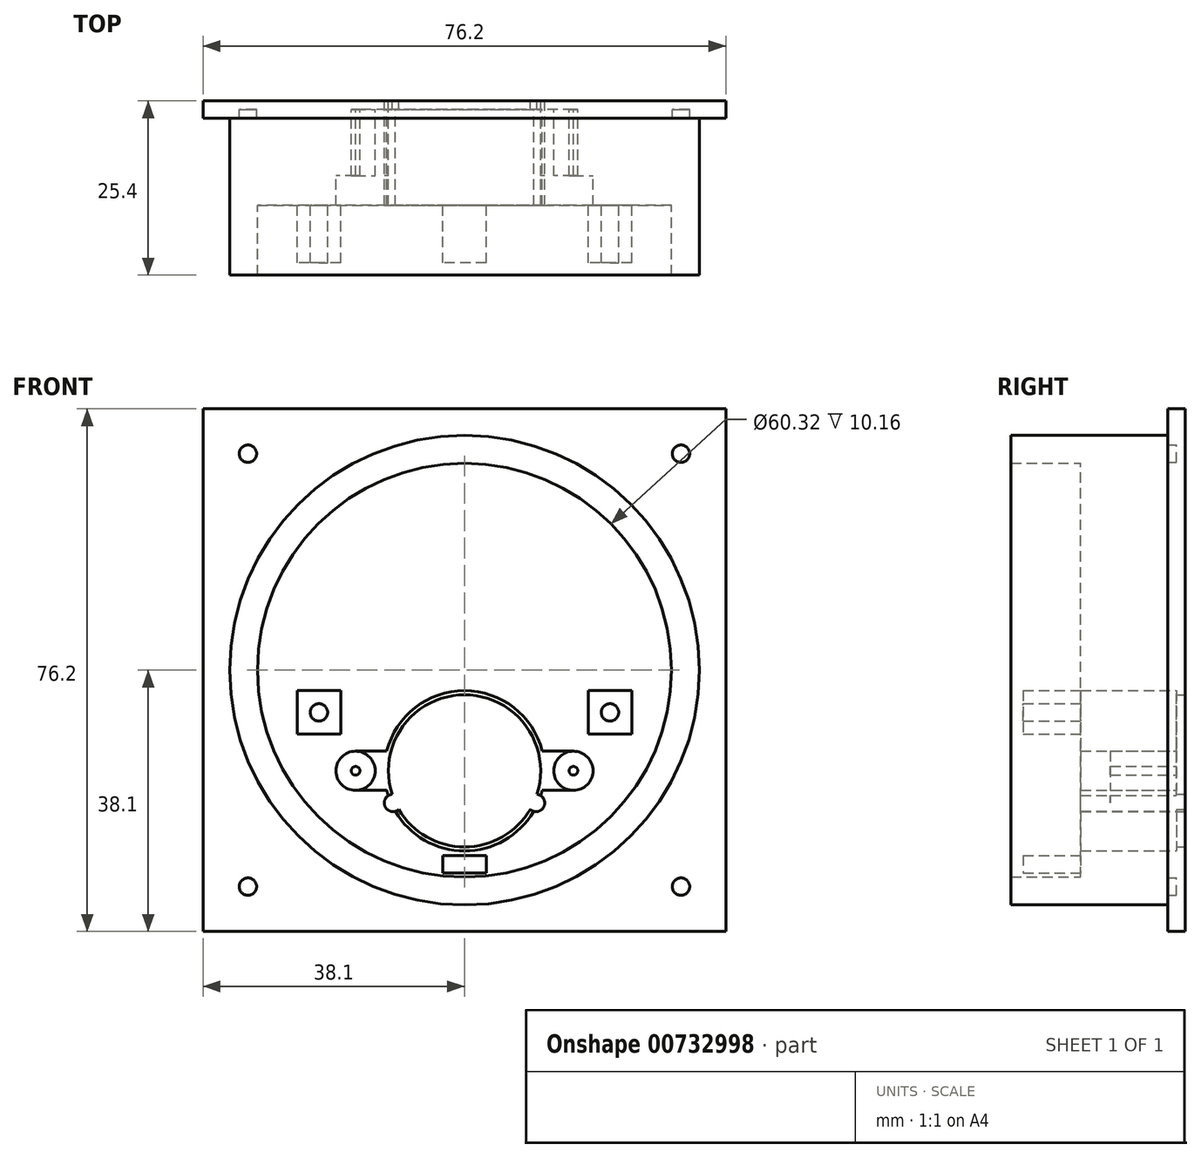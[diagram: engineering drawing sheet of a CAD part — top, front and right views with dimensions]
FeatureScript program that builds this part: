
annotation { "Feature Type Name" : "Feature", "Feature Type Description" : "" }
export const myFeature = defineFeature(function(context is Context, id is Id, definition is map)
    precondition{}
    {
        {
            var Q0;
            Q0=qCreatedBy(makeId("Front.planeOp"),FACE);
            var sketch = newSketch(context, id + "F0", { "sketchPlane" : qUnion([Q0])});
            skCircle(sketch, "E0", {"center": v(0, 0) * mm, "radius": 30.16 * mm});
            skCircle(sketch, "E1", {"center": v(0, -14.67) * mm, "radius": 11.68 * mm});
            skCircle(sketch, "E2", {"center": v(-15.88, -14.67) * mm, "radius": 2.86 * mm});
            skCircle(sketch, "E3", {"center": v(15.88, -14.67) * mm, "radius": 2.86 * mm});
            skPoint(sketch, "E4", {"position": v(-10.41, -19.34) * mm});
            skPoint(sketch, "E5", {"position": v(10.41, -19.34) * mm});
            skLineSegment(sketch, "E6.bottom", {"start": v(15.88, -11.81) * mm, "end": v(-15.88, -11.81) * mm});
            skLineSegment(sketch, "E6.top", {"start": v(15.88, -17.53) * mm, "end": v(-15.88, -17.53) * mm});
            skLineSegment(sketch, "E6.left", {"start": v(15.88, -11.81) * mm, "end": v(15.88, -17.53) * mm});
            skLineSegment(sketch, "E6.right", {"start": v(-15.88, -11.81) * mm, "end": v(-15.88, -17.53) * mm});
            skLineSegment(sketch, "E7.bottom", {"start": v(38.1, 38.1) * mm, "end": v(-38.1, 38.1) * mm});
            skLineSegment(sketch, "E7.top", {"start": v(38.1, -38.1) * mm, "end": v(-38.1, -38.1) * mm});
            skLineSegment(sketch, "E7.left", {"start": v(38.1, 38.1) * mm, "end": v(38.1, -38.1) * mm});
            skLineSegment(sketch, "E7.right", {"start": v(-38.1, 38.1) * mm, "end": v(-38.1, -38.1) * mm});
            skPoint(sketch, "E8", {"position": v(-31.56, 31.56) * mm});
            skPoint(sketch, "E9", {"position": v(31.56, 31.56) * mm});
            skPoint(sketch, "E10", {"position": v(31.56, -31.56) * mm});
            skPoint(sketch, "E11", {"position": v(-31.56, -31.56) * mm});
            skSolve(sketch);
        }
        {
            var Q0;
            Q0=makeQuery(id+"F0.imprint","IMPRINT",FACE,{"disambiguationData":[TD([[makeQuery(id+"F0.imprint","IMPRINT",EDGE,{"derivedFrom":sQuery(id+"F0.wireOp",EDGE,"E0")}),1.0]])]});
            extrude(context, id + "F1", {"entities" : qUnion([Q0]), "depth" : 15.24 * mm, "offsetDistance" : 25.4 * mm});
        }
        {
            var Q0;
            Q0=sQuery(id+"F0.wireOp",VERTEX,"E4");
            var Q1;
            Q1=sQuery(id+"F0.wireOp",VERTEX,"E5");
            var Q2;
            Q2=makeQuery(id+"F1.opExtrude","SWEPT_BODY",BODY,{"disambiguationData":[OSD([sQuery(id+"F0.wireOp",EDGE,"E0"),sQuery(id+"F0.wireOp",EDGE,"E1"),sQuery(id+"F0.wireOp",EDGE,"E2"),sQuery(id+"F0.wireOp",EDGE,"E3"),sQuery(id+"F0.wireOp",EDGE,"AQVEhfqM-bFfV-HZmN-Bbqf-DNwuXJOXuMRX.top"),sQuery(id+"F0.wireOp",EDGE,"FJdyEDiO-yEiY-Ot4F-tMeN-V1f38BCFD4gc.top")])]});
            hole(context, id + "F2", {"style" : HoleStyle.SIMPLE, "endStyle" : HoleEndStyle.THROUGH, "oppositeDirection" : true, "holeDiameter" : 2.54 * mm, "majorDiameter" : 6.35 * mm, "isTappedThrough" : true, "tappedDepth" : 12.7 * mm, "tapClearance" : 3, "locations" : qUnion([Q0, Q1]), "scope" : qUnion([Q2])});
        }
        {
            var Q0;
            {var subQ4=sQuery(id+"F0.wireOp",EDGE,"E6.right");Q0=makeQuery(id+"F0.imprint","IMPRINT",FACE,{"disambiguationData":[TD([[makeQuery(id+"F0.imprint","IMPRINT",EDGE,{"derivedFrom":subQ4}),1.0]])]});}
            var Q1;
            {var subQ0=sQuery(id+"F0.wireOp",EDGE,"E6.right");Q1=makeQuery(id+"F0.imprint","IMPRINT",FACE,{"disambiguationData":[TD([[makeQuery(id+"F0.imprint","IMPRINT",EDGE,{"derivedFrom":subQ0}),-1.0]])]});}
            var Q2;
            {var subQ4=sQuery(id+"F0.wireOp",EDGE,"E6.left");Q2=makeQuery(id+"F0.imprint","IMPRINT",FACE,{"disambiguationData":[TD([[makeQuery(id+"F0.imprint","IMPRINT",EDGE,{"derivedFrom":subQ4}),-1.0]])]});}
            var Q3;
            {var subQ0=sQuery(id+"F0.wireOp",EDGE,"E6.left");Q3=makeQuery(id+"F0.imprint","IMPRINT",FACE,{"disambiguationData":[TD([[makeQuery(id+"F0.imprint","IMPRINT",EDGE,{"derivedFrom":subQ0}),1.0]])]});}
            var Q4;
            {var subQ0=sQuery(id+"F0.wireOp",EDGE,"E6.bottom");var subQ1=sQuery(id+"F0.wireOp",EDGE,"E1");var subQ2=makeQuery(id+"F0.imprint","INTERSECT",VERTEX,{"disambiguationData":[OD(0.0)],"derivedFrom":[subQ1,subQ0]});Q4=makeQuery(id+"F0.imprint","IMPRINT",FACE,{"disambiguationData":[TD([[makeQuery(id+"F0.imprint","IMPRINT",EDGE,{"disambiguationData":[TD([[subQ2,-1.0]])],"derivedFrom":subQ1}),-1.0]])]});}
            var Q5;
            {var subQ0=sQuery(id+"F0.wireOp",EDGE,"E6.bottom");var subQ1=sQuery(id+"F0.wireOp",EDGE,"E1");var subQ2=makeQuery(id+"F0.imprint","INTERSECT",VERTEX,{"disambiguationData":[OD(1.0)],"derivedFrom":[subQ1,subQ0]});Q5=makeQuery(id+"F0.imprint","IMPRINT",FACE,{"disambiguationData":[TD([[makeQuery(id+"F0.imprint","IMPRINT",EDGE,{"disambiguationData":[TD([[subQ2,1.0]])],"derivedFrom":subQ1}),-1.0]])]});}
            extrude(context, id + "F3", {"entities" : qUnion([Q0, Q1, Q2, Q3, Q4, Q5]), "operationType" : NewBodyOperationType.ADD, "depth" : 10.92 * mm, "offsetDistance" : 25.4 * mm});
        }
        {
            var Q0;
            Q0=sQuery(id+"F0.wireOp",VERTEX,"E2.center");
            var Q1;
            Q1=sQuery(id+"F0.wireOp",VERTEX,"E3.center");
            var Q2;
            Q2=makeQuery(id+"F1.opExtrude","SWEPT_BODY",BODY,{"disambiguationData":[OSD([sQuery(id+"F0.wireOp",EDGE,"E0"),sQuery(id+"F0.wireOp",EDGE,"E1"),sQuery(id+"F0.wireOp",EDGE,"E2"),sQuery(id+"F0.wireOp",EDGE,"E3"),sQuery(id+"F0.wireOp",EDGE,"E6.bottom"),sQuery(id+"F0.wireOp",EDGE,"E6.top")])]});
            hole(context, id + "F4", {"style" : HoleStyle.SIMPLE, "endStyle" : HoleEndStyle.THROUGH, "oppositeDirection" : true, "holeDiameter" : 1.27 * mm, "majorDiameter" : 6.35 * mm, "isTappedThrough" : true, "tappedDepth" : 12.7 * mm, "tapClearance" : 3, "locations" : qUnion([Q0, Q1]), "scope" : qUnion([Q2])});
        }
        {
            var Q0;
            Q0=qCreatedBy(makeId("Front.planeOp"),FACE);
            var sketch = newSketch(context, id + "F5", { "sketchPlane" : qUnion([Q0])});
            skCircle(sketch, "E12", {"center": v(0, 0) * mm, "radius": 30.16 * mm});
            skCircle(sketch, "E13", {"center": v(0, 0) * mm, "radius": 34.23 * mm});
            skSolve(sketch);
        }
        {
            var Q0;
            Q0 = qSketchRegion(id + "F5", true);
            extrude(context, id + "F6", {"entities" : qUnion([Q0]), "operationType" : NewBodyOperationType.ADD, "depth" : 25.4 * mm, "offsetDistance" : 25.4 * mm});
        }
        {
            var Q0;
            Q0=qCreatedBy(makeId("Front.planeOp"),FACE);
            cPlane(context, id + "F7", {"entities" : qUnion([Q0]), "cplaneType" : CPlaneType.OFFSET, "offset" : 15.24 * mm, "width" : 152.4 * mm, "height" : 152.4 * mm});
        }
        {
            var Q0;
            Q0=qCreatedBy(id+"F7.planeOp",FACE);
            var sketch = newSketch(context, id + "F8", { "sketchPlane" : qUnion([Q0])});
            skLineSegment(sketch, "E14.bottom", {"start": v(3.18, -27.01) * mm, "end": v(-3.18, -27.01) * mm});
            skLineSegment(sketch, "E14.top", {"start": v(3.18, -29.55) * mm, "end": v(-3.18, -29.55) * mm});
            skLineSegment(sketch, "E14.left", {"start": v(3.18, -27.01) * mm, "end": v(3.18, -29.55) * mm});
            skLineSegment(sketch, "E14.right", {"start": v(-3.18, -27.01) * mm, "end": v(-3.18, -29.55) * mm});
            skPoint(sketch, "E14.middle", {"position": v(0, -28.28) * mm});
            skLineSegment(sketch, "E15.bottom", {"start": v(-18.03, -2.98) * mm, "end": v(-24.38, -2.98) * mm});
            skLineSegment(sketch, "E15.top", {"start": v(-18.03, -9.33) * mm, "end": v(-24.38, -9.33) * mm});
            skLineSegment(sketch, "E15.left", {"start": v(-18.03, -2.98) * mm, "end": v(-18.03, -9.33) * mm});
            skLineSegment(sketch, "E15.right", {"start": v(-24.38, -2.98) * mm, "end": v(-24.38, -9.33) * mm});
            skPoint(sketch, "E15.middle", {"position": v(-21.2, -6.16) * mm});
            skLineSegment(sketch, "E16.bottom", {"start": v(24.38, -9.33) * mm, "end": v(18.03, -9.33) * mm});
            skLineSegment(sketch, "E16.top", {"start": v(24.38, -2.98) * mm, "end": v(18.03, -2.98) * mm});
            skLineSegment(sketch, "E16.left", {"start": v(24.38, -9.33) * mm, "end": v(24.38, -2.98) * mm});
            skLineSegment(sketch, "E16.right", {"start": v(18.03, -9.33) * mm, "end": v(18.03, -2.98) * mm});
            skPoint(sketch, "E16.middle", {"position": v(21.2, -6.16) * mm});
            skSolve(sketch);
        }
        {
            var Q0;
            Q0 = qSketchRegion(id + "F8", true);
            extrude(context, id + "F9", {"entities" : qUnion([Q0]), "operationType" : NewBodyOperationType.ADD, "depth" : 8.38 * mm, "offsetDistance" : 25.4 * mm});
        }
        {
            var Q0;
            Q0=sQuery(id+"F8.wireOp",VERTEX,"E15.middle");
            var Q1;
            Q1=sQuery(id+"F8.wireOp",VERTEX,"E16.middle");
            var Q2;
            Q2=makeQuery(id+"F1.opExtrude","SWEPT_BODY",BODY,{"disambiguationData":[OSD([sQuery(id+"F0.wireOp",EDGE,"E0"),sQuery(id+"F0.wireOp",EDGE,"E1"),sQuery(id+"F0.wireOp",EDGE,"E2"),sQuery(id+"F0.wireOp",EDGE,"E3"),sQuery(id+"F0.wireOp",EDGE,"E6.bottom"),sQuery(id+"F0.wireOp",EDGE,"E6.top")])]});
            hole(context, id + "F10", {"style" : HoleStyle.SIMPLE, "endStyle" : HoleEndStyle.THROUGH, "oppositeDirection" : true, "holeDiameter" : 2.54 * mm, "majorDiameter" : 6.35 * mm, "isTappedThrough" : true, "tappedDepth" : 12.7 * mm, "tapClearance" : 3, "locations" : qUnion([Q0, Q1]), "scope" : qUnion([Q2])});
        }
        {
            var Q0;
            Q0=makeQuery(id+"F0.imprint","IMPRINT",FACE,{"disambiguationData":[TD([[makeQuery(id+"F0.imprint","IMPRINT",EDGE,{"derivedFrom":sQuery(id+"F0.wireOp",EDGE,"E0")}),-1.0]])]});
            extrude(context, id + "F11", {"entities" : qUnion([Q0]), "operationType" : NewBodyOperationType.ADD, "depth" : 2.54 * mm, "offsetDistance" : 25.4 * mm});
        }
        {
            var Q0;
            Q0=sQuery(id+"F0.wireOp",VERTEX,"E10");
            var Q1;
            Q1=sQuery(id+"F0.wireOp",VERTEX,"E11");
            var Q2;
            Q2=sQuery(id+"F0.wireOp",VERTEX,"E8");
            var Q3;
            Q3=sQuery(id+"F0.wireOp",VERTEX,"E9");
            var Q4;
            Q4=makeQuery(id+"F1.opExtrude","SWEPT_BODY",BODY,{"disambiguationData":[OSD([sQuery(id+"F0.wireOp",EDGE,"E0"),sQuery(id+"F0.wireOp",EDGE,"E1"),sQuery(id+"F0.wireOp",EDGE,"E2"),sQuery(id+"F0.wireOp",EDGE,"E3"),sQuery(id+"F0.wireOp",EDGE,"E6.bottom"),sQuery(id+"F0.wireOp",EDGE,"E6.top")])]});
            hole(context, id + "F12", {"style" : HoleStyle.SIMPLE, "endStyle" : HoleEndStyle.THROUGH, "oppositeDirection" : true, "holeDiameter" : 2.54 * mm, "majorDiameter" : 6.35 * mm, "isTappedThrough" : true, "tappedDepth" : 12.7 * mm, "tapClearance" : 3, "locations" : qUnion([Q0, Q1, Q2, Q3]), "scope" : qUnion([Q4])});
        }
        {
            var Q0;
            Q0=qCreatedBy(makeId("Front.planeOp"),FACE);
            var sketch = newSketch(context, id + "F13", { "sketchPlane" : qUnion([Q0])});
            skLineSegment(sketch, "E17.bottom", {"start": v(38.1, 38.1) * mm, "end": v(-38.1, 38.1) * mm});
            skLineSegment(sketch, "E17.top", {"start": v(38.1, -38.1) * mm, "end": v(-38.1, -38.1) * mm});
            skLineSegment(sketch, "E17.left", {"start": v(38.1, 38.1) * mm, "end": v(38.1, -38.1) * mm});
            skLineSegment(sketch, "E17.right", {"start": v(-38.1, 38.1) * mm, "end": v(-38.1, -38.1) * mm});
            skCircle(sketch, "E18", {"center": v(0, -14.68) * mm, "radius": 11.1 * mm});
            skPoint(sketch, "E19", {"position": v(10.41, -19.35) * mm});
            skPoint(sketch, "E20", {"position": v(-10.41, -19.35) * mm});
            skSolve(sketch);
        }
        {
            var Q0;
            Q0 = qSketchRegion(id + "F13", true);
            extrude(context, id + "F14", {"entities" : qUnion([Q0]), "operationType" : NewBodyOperationType.ADD, "depth" : 1.27 * mm, "offsetDistance" : 25.4 * mm});
        }
        {
            var Q0;
            Q0=sQuery(id+"F13.wireOp",VERTEX,"E19");
            var Q1;
            Q1=sQuery(id+"F13.wireOp",VERTEX,"E20");
            var Q2;
            Q2=makeQuery(id+"F1.opExtrude","SWEPT_BODY",BODY,{"disambiguationData":[OSD([sQuery(id+"F0.wireOp",EDGE,"E0"),sQuery(id+"F0.wireOp",EDGE,"E1"),sQuery(id+"F0.wireOp",EDGE,"E2"),sQuery(id+"F0.wireOp",EDGE,"E3"),sQuery(id+"F0.wireOp",EDGE,"E6.bottom"),sQuery(id+"F0.wireOp",EDGE,"E6.top")])]});
            hole(context, id + "F15", {"style" : HoleStyle.SIMPLE, "endStyle" : HoleEndStyle.THROUGH, "oppositeDirection" : true, "holeDiameter" : 2.54 * mm, "majorDiameter" : 6.35 * mm, "isTappedThrough" : true, "tappedDepth" : 12.7 * mm, "tapClearance" : 3, "locations" : qUnion([Q0, Q1]), "scope" : qUnion([Q2])});
        }
    });
